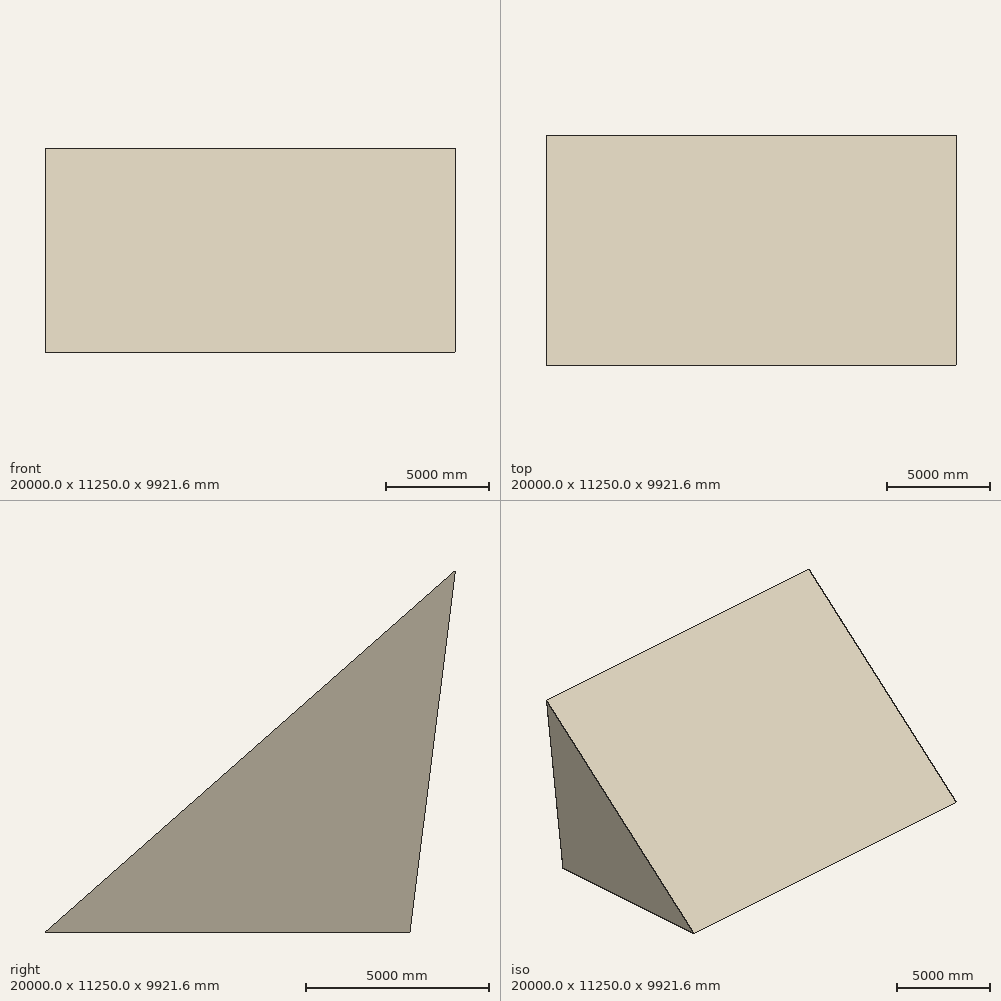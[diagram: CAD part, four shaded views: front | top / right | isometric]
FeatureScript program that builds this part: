
annotation { "Feature Type Name" : "Feature", "Feature Type Description" : "" }
export const myFeature = defineFeature(function(context is Context, id is Id, definition is map)
    precondition{}
    {
        {
            var Q0;
            Q0=qCreatedBy(makeId("Right.planeOp"),FACE);
            var sketch = newSketch(context, id + "F0", { "sketchPlane" : qUnion([Q0])});
            skLineSegment(sketch, "E0", {"start": v(4239.37, 3447.6) * mm, "end": v(-7010.63, -6473.97) * mm});
            skLineSegment(sketch, "E1", {"start": v(-7010.63, -6473.97) * mm, "end": v(2989.37, -6473.97) * mm});
            skLineSegment(sketch, "E2", {"start": v(2989.37, -6473.97) * mm, "end": v(4239.37, 3447.6) * mm});
            skSolve(sketch);
        }
        {
            var Q0;
            Q0 = qSketchRegion(id + "F0", true);
            extrude(context, id + "F1", {"entities" : qUnion([Q0]), "oppositeDirection" : true, "depth" : 20000 * mm, "offsetDistance" : 25 * mm});
        }
    });
